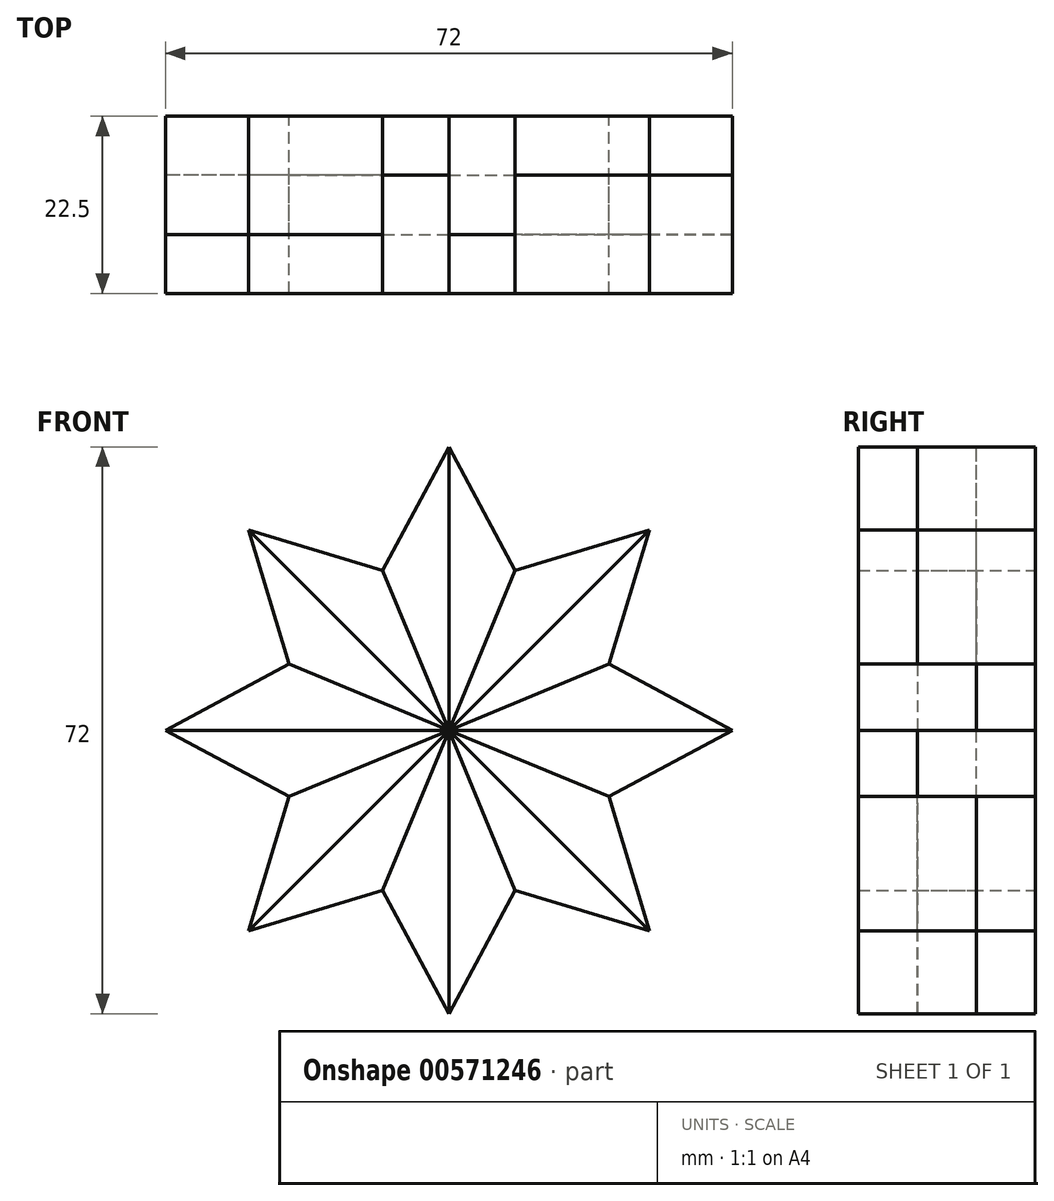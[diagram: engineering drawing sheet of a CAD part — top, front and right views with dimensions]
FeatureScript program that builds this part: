
annotation { "Feature Type Name" : "Feature", "Feature Type Description" : "" }
export const myFeature = defineFeature(function(context is Context, id is Id, definition is map)
    precondition{}
    {
        {
            var Q0;
            Q0=qCreatedBy(makeId("Front.planeOp"),FACE);
            var sketch = newSketch(context, id + "F0", { "sketchPlane" : qUnion([Q0])});
            skLineSegment(sketch, "E0", {"start": v(0, 0) * mm, "end": v(0, 36) * mm});
            skLineSegment(sketch, "E1", {"start": v(0, 0) * mm, "end": v(8.42, 20.33) * mm});
            skLineSegment(sketch, "E2", {"start": v(0, 36) * mm, "end": v(8.42, 20.33) * mm});
            skLineSegment(sketch, "E3", {"start": v(-8.42, 20.33) * mm, "end": v(0, 0) * mm});
            skLineSegment(sketch, "E4", {"start": v(-8.42, 20.33) * mm, "end": v(0, 36) * mm});
            skLineSegment(sketch, "E5", {"start": v(0.76, 1.83) * mm, "end": v(0.76, 34.59) * mm});
            skLineSegment(sketch, "E6.0.1.0", {"start": v(1.95, 4.7) * mm, "end": v(1.95, 32.37) * mm});
            skLineSegment(sketch, "E6.0.2.0", {"start": v(3.14, 7.57) * mm, "end": v(3.14, 30.16) * mm});
            skLineSegment(sketch, "E6.0.3.0", {"start": v(4.33, 10.44) * mm, "end": v(4.33, 27.95) * mm});
            skLineSegment(sketch, "E6.0.4.0", {"start": v(5.51, 13.31) * mm, "end": v(5.51, 25.73) * mm});
            skLineSegment(sketch, "E6.0.5.0", {"start": v(6.7, 16.18) * mm, "end": v(6.7, 23.52) * mm});
            skLineSegment(sketch, "E6.0.6.0", {"start": v(7.9, 19.05) * mm, "end": v(7.9, 21.3) * mm});
            skLineSegment(sketch, "E7.1.0", {"start": v(-5.51, 13.31) * mm, "end": v(-14.3, 22.1) * mm});
            skLineSegment(sketch, "E7.1.1", {"start": v(-6.7, 16.18) * mm, "end": v(-11.9, 21.37) * mm});
            skLineSegment(sketch, "E7.1.2", {"start": v(0, 0) * mm, "end": v(-8.42, 20.33) * mm});
            skLineSegment(sketch, "E7.1.3", {"start": v(-4.33, 10.44) * mm, "end": v(-16.7, 22.82) * mm});
            skLineSegment(sketch, "E7.1.4", {"start": v(-3.14, 7.57) * mm, "end": v(-19.1, 23.54) * mm});
            skLineSegment(sketch, "E7.1.5", {"start": v(-25.46, 25.46) * mm, "end": v(-8.42, 20.33) * mm});
            skLineSegment(sketch, "E7.1.6", {"start": v(-20.33, 8.42) * mm, "end": v(0, 0) * mm});
            skLineSegment(sketch, "E7.1.7", {"start": v(-1.95, 4.7) * mm, "end": v(-21.52, 24.27) * mm});
            skLineSegment(sketch, "E7.1.8", {"start": v(-0.76, 1.83) * mm, "end": v(-23.92, 25) * mm});
            skLineSegment(sketch, "E7.1.9", {"start": v(-20.33, 8.42) * mm, "end": v(-25.46, 25.46) * mm});
            skLineSegment(sketch, "E7.1.10", {"start": v(0, 0) * mm, "end": v(-25.46, 25.46) * mm});
            skLineSegment(sketch, "E7.1.11", {"start": v(-7.9, 19.05) * mm, "end": v(-9.49, 20.65) * mm});
            skLineSegment(sketch, "E7.2.0", {"start": v(-13.31, 5.51) * mm, "end": v(-25.73, 5.51) * mm});
            skLineSegment(sketch, "E7.2.1", {"start": v(-16.18, 6.7) * mm, "end": v(-23.52, 6.7) * mm});
            skLineSegment(sketch, "E7.2.2", {"start": v(0, 0) * mm, "end": v(-20.33, 8.42) * mm});
            skLineSegment(sketch, "E7.2.3", {"start": v(-10.44, 4.33) * mm, "end": v(-27.95, 4.33) * mm});
            skLineSegment(sketch, "E7.2.4", {"start": v(-7.57, 3.14) * mm, "end": v(-30.16, 3.14) * mm});
            skLineSegment(sketch, "E7.2.5", {"start": v(-36, 0) * mm, "end": v(-20.33, 8.42) * mm});
            skLineSegment(sketch, "E7.2.6", {"start": v(-20.33, -8.42) * mm, "end": v(0, 0) * mm});
            skLineSegment(sketch, "E7.2.7", {"start": v(-4.7, 1.95) * mm, "end": v(-32.37, 1.95) * mm});
            skLineSegment(sketch, "E7.2.8", {"start": v(-1.83, 0.76) * mm, "end": v(-34.59, 0.76) * mm});
            skLineSegment(sketch, "E7.2.9", {"start": v(-20.33, -8.42) * mm, "end": v(-36, 0) * mm});
            skLineSegment(sketch, "E7.2.10", {"start": v(0, 0) * mm, "end": v(-36, 0) * mm});
            skLineSegment(sketch, "E7.2.11", {"start": v(-19.05, 7.9) * mm, "end": v(-21.3, 7.9) * mm});
            skLineSegment(sketch, "E7.3.0", {"start": v(-13.31, -5.51) * mm, "end": v(-22.1, -14.3) * mm});
            skLineSegment(sketch, "E7.3.1", {"start": v(-16.18, -6.7) * mm, "end": v(-21.37, -11.9) * mm});
            skLineSegment(sketch, "E7.3.2", {"start": v(0, 0) * mm, "end": v(-20.33, -8.42) * mm});
            skLineSegment(sketch, "E7.3.3", {"start": v(-10.44, -4.33) * mm, "end": v(-22.82, -16.7) * mm});
            skLineSegment(sketch, "E7.3.4", {"start": v(-7.57, -3.14) * mm, "end": v(-23.54, -19.1) * mm});
            skLineSegment(sketch, "E7.3.5", {"start": v(-25.46, -25.46) * mm, "end": v(-20.33, -8.42) * mm});
            skLineSegment(sketch, "E7.3.6", {"start": v(-8.42, -20.33) * mm, "end": v(0, 0) * mm});
            skLineSegment(sketch, "E7.3.7", {"start": v(-4.7, -1.95) * mm, "end": v(-24.27, -21.52) * mm});
            skLineSegment(sketch, "E7.3.8", {"start": v(-1.83, -0.76) * mm, "end": v(-25, -23.92) * mm});
            skLineSegment(sketch, "E7.3.9", {"start": v(-8.42, -20.33) * mm, "end": v(-25.46, -25.46) * mm});
            skLineSegment(sketch, "E7.3.10", {"start": v(0, 0) * mm, "end": v(-25.46, -25.46) * mm});
            skLineSegment(sketch, "E7.3.11", {"start": v(-19.05, -7.9) * mm, "end": v(-20.65, -9.49) * mm});
            skLineSegment(sketch, "E7.4.0", {"start": v(-5.51, -13.31) * mm, "end": v(-5.51, -25.73) * mm});
            skLineSegment(sketch, "E7.4.1", {"start": v(-6.7, -16.18) * mm, "end": v(-6.7, -23.52) * mm});
            skLineSegment(sketch, "E7.4.2", {"start": v(0, 0) * mm, "end": v(-8.42, -20.33) * mm});
            skLineSegment(sketch, "E7.4.3", {"start": v(-4.33, -10.44) * mm, "end": v(-4.33, -27.95) * mm});
            skLineSegment(sketch, "E7.4.4", {"start": v(-3.14, -7.57) * mm, "end": v(-3.14, -30.16) * mm});
            skLineSegment(sketch, "E7.4.5", {"start": v(0, -36) * mm, "end": v(-8.42, -20.33) * mm});
            skLineSegment(sketch, "E7.4.6", {"start": v(8.42, -20.33) * mm, "end": v(0, 0) * mm});
            skLineSegment(sketch, "E7.4.7", {"start": v(-1.95, -4.7) * mm, "end": v(-1.95, -32.37) * mm});
            skLineSegment(sketch, "E7.4.8", {"start": v(-0.76, -1.83) * mm, "end": v(-0.76, -34.59) * mm});
            skLineSegment(sketch, "E7.4.9", {"start": v(8.42, -20.33) * mm, "end": v(0, -36) * mm});
            skLineSegment(sketch, "E7.4.10", {"start": v(0, 0) * mm, "end": v(0, -36) * mm});
            skLineSegment(sketch, "E7.4.11", {"start": v(-7.9, -19.05) * mm, "end": v(-7.9, -21.3) * mm});
            skLineSegment(sketch, "E7.5.0", {"start": v(5.51, -13.31) * mm, "end": v(14.3, -22.1) * mm});
            skLineSegment(sketch, "E7.5.1", {"start": v(6.7, -16.18) * mm, "end": v(11.9, -21.37) * mm});
            skLineSegment(sketch, "E7.5.2", {"start": v(0, 0) * mm, "end": v(8.42, -20.33) * mm});
            skLineSegment(sketch, "E7.5.3", {"start": v(4.33, -10.44) * mm, "end": v(16.7, -22.82) * mm});
            skLineSegment(sketch, "E7.5.4", {"start": v(3.14, -7.57) * mm, "end": v(19.1, -23.54) * mm});
            skLineSegment(sketch, "E7.5.5", {"start": v(25.46, -25.46) * mm, "end": v(8.42, -20.33) * mm});
            skLineSegment(sketch, "E7.5.6", {"start": v(20.33, -8.42) * mm, "end": v(0, 0) * mm});
            skLineSegment(sketch, "E7.5.7", {"start": v(1.95, -4.7) * mm, "end": v(21.52, -24.27) * mm});
            skLineSegment(sketch, "E7.5.8", {"start": v(0.76, -1.83) * mm, "end": v(23.92, -25) * mm});
            skLineSegment(sketch, "E7.5.9", {"start": v(20.33, -8.42) * mm, "end": v(25.46, -25.46) * mm});
            skLineSegment(sketch, "E7.5.10", {"start": v(0, 0) * mm, "end": v(25.46, -25.46) * mm});
            skLineSegment(sketch, "E7.5.11", {"start": v(7.9, -19.05) * mm, "end": v(9.49, -20.65) * mm});
            skLineSegment(sketch, "E7.6.0", {"start": v(13.31, -5.51) * mm, "end": v(25.73, -5.51) * mm});
            skLineSegment(sketch, "E7.6.1", {"start": v(16.18, -6.7) * mm, "end": v(23.52, -6.7) * mm});
            skLineSegment(sketch, "E7.6.2", {"start": v(0, 0) * mm, "end": v(20.33, -8.42) * mm});
            skLineSegment(sketch, "E7.6.3", {"start": v(10.44, -4.33) * mm, "end": v(27.95, -4.33) * mm});
            skLineSegment(sketch, "E7.6.4", {"start": v(7.57, -3.14) * mm, "end": v(30.16, -3.14) * mm});
            skLineSegment(sketch, "E7.6.5", {"start": v(36, 0) * mm, "end": v(20.33, -8.42) * mm});
            skLineSegment(sketch, "E7.6.6", {"start": v(20.33, 8.42) * mm, "end": v(0, 0) * mm});
            skLineSegment(sketch, "E7.6.7", {"start": v(4.7, -1.95) * mm, "end": v(32.37, -1.95) * mm});
            skLineSegment(sketch, "E7.6.8", {"start": v(1.83, -0.76) * mm, "end": v(34.59, -0.76) * mm});
            skLineSegment(sketch, "E7.6.9", {"start": v(20.33, 8.42) * mm, "end": v(36, 0) * mm});
            skLineSegment(sketch, "E7.6.10", {"start": v(0, 0) * mm, "end": v(36, 0) * mm});
            skLineSegment(sketch, "E7.6.11", {"start": v(19.05, -7.9) * mm, "end": v(21.3, -7.9) * mm});
            skLineSegment(sketch, "E7.7.0", {"start": v(13.31, 5.51) * mm, "end": v(22.1, 14.3) * mm});
            skLineSegment(sketch, "E7.7.1", {"start": v(16.18, 6.7) * mm, "end": v(21.37, 11.9) * mm});
            skLineSegment(sketch, "E7.7.2", {"start": v(0, 0) * mm, "end": v(20.33, 8.42) * mm});
            skLineSegment(sketch, "E7.7.3", {"start": v(10.44, 4.33) * mm, "end": v(22.82, 16.7) * mm});
            skLineSegment(sketch, "E7.7.4", {"start": v(7.57, 3.14) * mm, "end": v(23.54, 19.1) * mm});
            skLineSegment(sketch, "E7.7.5", {"start": v(25.46, 25.46) * mm, "end": v(20.33, 8.42) * mm});
            skLineSegment(sketch, "E7.7.6", {"start": v(8.42, 20.33) * mm, "end": v(0, 0) * mm});
            skLineSegment(sketch, "E7.7.7", {"start": v(4.7, 1.95) * mm, "end": v(24.27, 21.52) * mm});
            skLineSegment(sketch, "E7.7.8", {"start": v(1.83, 0.76) * mm, "end": v(25, 23.92) * mm});
            skLineSegment(sketch, "E7.7.9", {"start": v(8.42, 20.33) * mm, "end": v(25.46, 25.46) * mm});
            skLineSegment(sketch, "E7.7.10", {"start": v(0, 0) * mm, "end": v(25.46, 25.46) * mm});
            skLineSegment(sketch, "E7.7.11", {"start": v(19.05, 7.9) * mm, "end": v(20.65, 9.49) * mm});
            skPoint(sketch, "E7.center", {"position": v(0, 0) * mm});
            skSolve(sketch);
        }
        {
            var Q0;
            {var subQ0=sQuery(id+"F0.wireOp",EDGE,"E7.7.7");Q0=makeQuery(id+"F0.imprint","IMPRINT",FACE,{"disambiguationData":[TD([[makeQuery(id+"F0.imprint","IMPRINT",EDGE,{"derivedFrom":subQ0}),1.0]])]});}
            var Q1;
            {var subQ0=sQuery(id+"F0.wireOp",EDGE,"E7.1.7");Q1=makeQuery(id+"F0.imprint","IMPRINT",FACE,{"disambiguationData":[TD([[makeQuery(id+"F0.imprint","IMPRINT",EDGE,{"derivedFrom":subQ0}),1.0]])]});}
            var Q2;
            {var subQ0=sQuery(id+"F0.wireOp",EDGE,"E7.3.7");Q2=makeQuery(id+"F0.imprint","IMPRINT",FACE,{"disambiguationData":[TD([[makeQuery(id+"F0.imprint","IMPRINT",EDGE,{"derivedFrom":subQ0}),1.0]])]});}
            var Q3;
            {var subQ0=sQuery(id+"F0.wireOp",EDGE,"E7.1.0");Q3=makeQuery(id+"F0.imprint","IMPRINT",FACE,{"disambiguationData":[TD([[makeQuery(id+"F0.imprint","IMPRINT",EDGE,{"derivedFrom":subQ0}),-1.0]])]});}
            var Q4;
            {var subQ0=sQuery(id+"F0.wireOp",EDGE,"E7.6.0");Q4=makeQuery(id+"F0.imprint","IMPRINT",FACE,{"disambiguationData":[TD([[makeQuery(id+"F0.imprint","IMPRINT",EDGE,{"derivedFrom":subQ0}),-1.0]])]});}
            var Q5;
            {var subQ0=sQuery(id+"F0.wireOp",EDGE,"E7.2.4");Q5=makeQuery(id+"F0.imprint","IMPRINT",FACE,{"disambiguationData":[TD([[makeQuery(id+"F0.imprint","IMPRINT",EDGE,{"derivedFrom":subQ0}),1.0]])]});}
            var Q6;
            {var subQ0=sQuery(id+"F0.wireOp",EDGE,"E7.5.0");Q6=makeQuery(id+"F0.imprint","IMPRINT",FACE,{"disambiguationData":[TD([[makeQuery(id+"F0.imprint","IMPRINT",EDGE,{"derivedFrom":subQ0}),-1.0]])]});}
            var Q7;
            {var subQ0=sQuery(id+"F0.wireOp",EDGE,"E7.5.1");Q7=makeQuery(id+"F0.imprint","IMPRINT",FACE,{"disambiguationData":[TD([[makeQuery(id+"F0.imprint","IMPRINT",EDGE,{"derivedFrom":subQ0}),-1.0]])]});}
            var Q8;
            {var subQ0=sQuery(id+"F0.wireOp",EDGE,"E7.2.3");Q8=makeQuery(id+"F0.imprint","IMPRINT",FACE,{"disambiguationData":[TD([[makeQuery(id+"F0.imprint","IMPRINT",EDGE,{"derivedFrom":subQ0}),1.0]])]});}
            var Q9;
            {var subQ2=sQuery(id+"F0.wireOp",EDGE,"E7.6.8");Q9=makeQuery(id+"F0.imprint","IMPRINT",FACE,{"disambiguationData":[TD([[makeQuery(id+"F0.imprint","IMPRINT",EDGE,{"derivedFrom":subQ2}),1.0]])]});}
            var Q10;
            {var subQ0=sQuery(id+"F0.wireOp",EDGE,"E7.4.0");Q10=makeQuery(id+"F0.imprint","IMPRINT",FACE,{"disambiguationData":[TD([[makeQuery(id+"F0.imprint","IMPRINT",EDGE,{"derivedFrom":subQ0}),1.0]])]});}
            var Q11;
            {var subQ0=sQuery(id+"F0.wireOp",EDGE,"E7.4.4");Q11=makeQuery(id+"F0.imprint","IMPRINT",FACE,{"disambiguationData":[TD([[makeQuery(id+"F0.imprint","IMPRINT",EDGE,{"derivedFrom":subQ0}),1.0]])]});}
            var Q12;
            {var subQ0=sQuery(id+"F0.wireOp",EDGE,"E7.2.0");Q12=makeQuery(id+"F0.imprint","IMPRINT",FACE,{"disambiguationData":[TD([[makeQuery(id+"F0.imprint","IMPRINT",EDGE,{"derivedFrom":subQ0}),-1.0]])]});}
            var Q13;
            {var subQ0=sQuery(id+"F0.wireOp",EDGE,"E7.1.1");Q13=makeQuery(id+"F0.imprint","IMPRINT",FACE,{"disambiguationData":[TD([[makeQuery(id+"F0.imprint","IMPRINT",EDGE,{"derivedFrom":subQ0}),-1.0]])]});}
            var Q14;
            {var subQ0=sQuery(id+"F0.wireOp",EDGE,"E7.6.4");Q14=makeQuery(id+"F0.imprint","IMPRINT",FACE,{"disambiguationData":[TD([[makeQuery(id+"F0.imprint","IMPRINT",EDGE,{"derivedFrom":subQ0}),1.0]])]});}
            var Q15;
            {var subQ2=sQuery(id+"F0.wireOp",EDGE,"E7.1.8");Q15=makeQuery(id+"F0.imprint","IMPRINT",FACE,{"disambiguationData":[TD([[makeQuery(id+"F0.imprint","IMPRINT",EDGE,{"derivedFrom":subQ2}),1.0]])]});}
            var Q16;
            {var subQ0=sQuery(id+"F0.wireOp",EDGE,"E7.2.0");Q16=makeQuery(id+"F0.imprint","IMPRINT",FACE,{"disambiguationData":[TD([[makeQuery(id+"F0.imprint","IMPRINT",EDGE,{"derivedFrom":subQ0}),1.0]])]});}
            var Q17;
            {var subQ2=sQuery(id+"F0.wireOp",EDGE,"E7.4.8");Q17=makeQuery(id+"F0.imprint","IMPRINT",FACE,{"disambiguationData":[TD([[makeQuery(id+"F0.imprint","IMPRINT",EDGE,{"derivedFrom":subQ2}),1.0]])]});}
            var Q18;
            {var subQ0=sQuery(id+"F0.wireOp",EDGE,"E7.4.1");Q18=makeQuery(id+"F0.imprint","IMPRINT",FACE,{"disambiguationData":[TD([[makeQuery(id+"F0.imprint","IMPRINT",EDGE,{"derivedFrom":subQ0}),-1.0]])]});}
            var Q19;
            {var subQ0=sQuery(id+"F0.wireOp",EDGE,"E7.6.7");Q19=makeQuery(id+"F0.imprint","IMPRINT",FACE,{"disambiguationData":[TD([[makeQuery(id+"F0.imprint","IMPRINT",EDGE,{"derivedFrom":subQ0}),1.0]])]});}
            var Q20;
            {var subQ0=sQuery(id+"F0.wireOp",EDGE,"E7.5.0");Q20=makeQuery(id+"F0.imprint","IMPRINT",FACE,{"disambiguationData":[TD([[makeQuery(id+"F0.imprint","IMPRINT",EDGE,{"derivedFrom":subQ0}),1.0]])]});}
            var Q21;
            {var subQ2=sQuery(id+"F0.wireOp",EDGE,"E7.7.8");Q21=makeQuery(id+"F0.imprint","IMPRINT",FACE,{"disambiguationData":[TD([[makeQuery(id+"F0.imprint","IMPRINT",EDGE,{"derivedFrom":subQ2}),1.0]])]});}
            var Q22;
            {var subQ0=sQuery(id+"F0.wireOp",EDGE,"E7.3.0");Q22=makeQuery(id+"F0.imprint","IMPRINT",FACE,{"disambiguationData":[TD([[makeQuery(id+"F0.imprint","IMPRINT",EDGE,{"derivedFrom":subQ0}),1.0]])]});}
            var Q23;
            {var subQ2=sQuery(id+"F0.wireOp",EDGE,"E7.5.8");Q23=makeQuery(id+"F0.imprint","IMPRINT",FACE,{"disambiguationData":[TD([[makeQuery(id+"F0.imprint","IMPRINT",EDGE,{"derivedFrom":subQ2}),1.0]])]});}
            var Q24;
            {var subQ0=sQuery(id+"F0.wireOp",EDGE,"E7.7.4");Q24=makeQuery(id+"F0.imprint","IMPRINT",FACE,{"disambiguationData":[TD([[makeQuery(id+"F0.imprint","IMPRINT",EDGE,{"derivedFrom":subQ0}),1.0]])]});}
            var Q25;
            {var subQ0=sQuery(id+"F0.wireOp",EDGE,"E7.1.3");Q25=makeQuery(id+"F0.imprint","IMPRINT",FACE,{"disambiguationData":[TD([[makeQuery(id+"F0.imprint","IMPRINT",EDGE,{"derivedFrom":subQ0}),1.0]])]});}
            var Q26;
            {var subQ0=sQuery(id+"F0.wireOp",EDGE,"E7.7.1");Q26=makeQuery(id+"F0.imprint","IMPRINT",FACE,{"disambiguationData":[TD([[makeQuery(id+"F0.imprint","IMPRINT",EDGE,{"derivedFrom":subQ0}),-1.0]])]});}
            var Q27;
            {var subQ0=sQuery(id+"F0.wireOp",EDGE,"E7.6.0");Q27=makeQuery(id+"F0.imprint","IMPRINT",FACE,{"disambiguationData":[TD([[makeQuery(id+"F0.imprint","IMPRINT",EDGE,{"derivedFrom":subQ0}),1.0]])]});}
            var Q28;
            {var subQ0=sQuery(id+"F0.wireOp",EDGE,"E7.3.0");Q28=makeQuery(id+"F0.imprint","IMPRINT",FACE,{"disambiguationData":[TD([[makeQuery(id+"F0.imprint","IMPRINT",EDGE,{"derivedFrom":subQ0}),-1.0]])]});}
            var Q29;
            {var subQ0=sQuery(id+"F0.wireOp",EDGE,"E7.1.4");Q29=makeQuery(id+"F0.imprint","IMPRINT",FACE,{"disambiguationData":[TD([[makeQuery(id+"F0.imprint","IMPRINT",EDGE,{"derivedFrom":subQ0}),1.0]])]});}
            var Q30;
            {var subQ0=sQuery(id+"F0.wireOp",EDGE,"E7.4.0");Q30=makeQuery(id+"F0.imprint","IMPRINT",FACE,{"disambiguationData":[TD([[makeQuery(id+"F0.imprint","IMPRINT",EDGE,{"derivedFrom":subQ0}),-1.0]])]});}
            var Q31;
            {var subQ0=sQuery(id+"F0.wireOp",EDGE,"E7.2.7");Q31=makeQuery(id+"F0.imprint","IMPRINT",FACE,{"disambiguationData":[TD([[makeQuery(id+"F0.imprint","IMPRINT",EDGE,{"derivedFrom":subQ0}),1.0]])]});}
            var Q32;
            {var subQ0=sQuery(id+"F0.wireOp",EDGE,"E7.6.1");Q32=makeQuery(id+"F0.imprint","IMPRINT",FACE,{"disambiguationData":[TD([[makeQuery(id+"F0.imprint","IMPRINT",EDGE,{"derivedFrom":subQ0}),-1.0]])]});}
            var Q33;
            {var subQ0=sQuery(id+"F0.wireOp",EDGE,"E7.7.0");Q33=makeQuery(id+"F0.imprint","IMPRINT",FACE,{"disambiguationData":[TD([[makeQuery(id+"F0.imprint","IMPRINT",EDGE,{"derivedFrom":subQ0}),1.0]])]});}
            var Q34;
            {var subQ0=sQuery(id+"F0.wireOp",EDGE,"E7.4.3");Q34=makeQuery(id+"F0.imprint","IMPRINT",FACE,{"disambiguationData":[TD([[makeQuery(id+"F0.imprint","IMPRINT",EDGE,{"derivedFrom":subQ0}),1.0]])]});}
            var Q35;
            {var subQ0=sQuery(id+"F0.wireOp",EDGE,"E7.3.3");Q35=makeQuery(id+"F0.imprint","IMPRINT",FACE,{"disambiguationData":[TD([[makeQuery(id+"F0.imprint","IMPRINT",EDGE,{"derivedFrom":subQ0}),1.0]])]});}
            var Q36;
            {var subQ0=sQuery(id+"F0.wireOp",EDGE,"E6.0.5.0");Q36=makeQuery(id+"F0.imprint","IMPRINT",FACE,{"disambiguationData":[TD([[makeQuery(id+"F0.imprint","IMPRINT",EDGE,{"derivedFrom":subQ0}),-1.0]])]});}
            var Q37;
            {var subQ0=sQuery(id+"F0.wireOp",EDGE,"E7.5.3");Q37=makeQuery(id+"F0.imprint","IMPRINT",FACE,{"disambiguationData":[TD([[makeQuery(id+"F0.imprint","IMPRINT",EDGE,{"derivedFrom":subQ0}),1.0]])]});}
            var Q38;
            {var subQ0=sQuery(id+"F0.wireOp",EDGE,"E7.7.3");Q38=makeQuery(id+"F0.imprint","IMPRINT",FACE,{"disambiguationData":[TD([[makeQuery(id+"F0.imprint","IMPRINT",EDGE,{"derivedFrom":subQ0}),1.0]])]});}
            var Q39;
            {var subQ0=sQuery(id+"F0.wireOp",EDGE,"E7.2.1");Q39=makeQuery(id+"F0.imprint","IMPRINT",FACE,{"disambiguationData":[TD([[makeQuery(id+"F0.imprint","IMPRINT",EDGE,{"derivedFrom":subQ0}),-1.0]])]});}
            var Q40;
            {var subQ0=sQuery(id+"F0.wireOp",EDGE,"E6.0.3.0");Q40=makeQuery(id+"F0.imprint","IMPRINT",FACE,{"disambiguationData":[TD([[makeQuery(id+"F0.imprint","IMPRINT",EDGE,{"derivedFrom":subQ0}),-1.0]])]});}
            var Q41;
            {var subQ0=sQuery(id+"F0.wireOp",EDGE,"E6.0.4.0");Q41=makeQuery(id+"F0.imprint","IMPRINT",FACE,{"disambiguationData":[TD([[makeQuery(id+"F0.imprint","IMPRINT",EDGE,{"derivedFrom":subQ0}),-1.0]])]});}
            var Q42;
            {var subQ0=sQuery(id+"F0.wireOp",EDGE,"E7.3.4");Q42=makeQuery(id+"F0.imprint","IMPRINT",FACE,{"disambiguationData":[TD([[makeQuery(id+"F0.imprint","IMPRINT",EDGE,{"derivedFrom":subQ0}),1.0]])]});}
            var Q43;
            {var subQ0=sQuery(id+"F0.wireOp",EDGE,"E5");Q43=makeQuery(id+"F0.imprint","IMPRINT",FACE,{"disambiguationData":[TD([[makeQuery(id+"F0.imprint","IMPRINT",EDGE,{"derivedFrom":subQ0}),-1.0]])]});}
            var Q44;
            {var subQ0=sQuery(id+"F0.wireOp",EDGE,"E6.0.1.0");Q44=makeQuery(id+"F0.imprint","IMPRINT",FACE,{"disambiguationData":[TD([[makeQuery(id+"F0.imprint","IMPRINT",EDGE,{"derivedFrom":subQ0}),-1.0]])]});}
            var Q45;
            {var subQ0=sQuery(id+"F0.wireOp",EDGE,"E7.5.7");Q45=makeQuery(id+"F0.imprint","IMPRINT",FACE,{"disambiguationData":[TD([[makeQuery(id+"F0.imprint","IMPRINT",EDGE,{"derivedFrom":subQ0}),1.0]])]});}
            var Q46;
            {var subQ0=sQuery(id+"F0.wireOp",EDGE,"E7.6.3");Q46=makeQuery(id+"F0.imprint","IMPRINT",FACE,{"disambiguationData":[TD([[makeQuery(id+"F0.imprint","IMPRINT",EDGE,{"derivedFrom":subQ0}),1.0]])]});}
            var Q47;
            {var subQ0=sQuery(id+"F0.wireOp",EDGE,"E7.3.1");Q47=makeQuery(id+"F0.imprint","IMPRINT",FACE,{"disambiguationData":[TD([[makeQuery(id+"F0.imprint","IMPRINT",EDGE,{"derivedFrom":subQ0}),-1.0]])]});}
            var Q48;
            {var subQ0=sQuery(id+"F0.wireOp",EDGE,"E6.0.2.0");Q48=makeQuery(id+"F0.imprint","IMPRINT",FACE,{"disambiguationData":[TD([[makeQuery(id+"F0.imprint","IMPRINT",EDGE,{"derivedFrom":subQ0}),-1.0]])]});}
            var Q49;
            {var subQ0=sQuery(id+"F0.wireOp",EDGE,"E7.5.4");Q49=makeQuery(id+"F0.imprint","IMPRINT",FACE,{"disambiguationData":[TD([[makeQuery(id+"F0.imprint","IMPRINT",EDGE,{"derivedFrom":subQ0}),1.0]])]});}
            var Q50;
            {var subQ2=sQuery(id+"F0.wireOp",EDGE,"E7.3.8");Q50=makeQuery(id+"F0.imprint","IMPRINT",FACE,{"disambiguationData":[TD([[makeQuery(id+"F0.imprint","IMPRINT",EDGE,{"derivedFrom":subQ2}),1.0]])]});}
            var Q51;
            {var subQ2=sQuery(id+"F0.wireOp",EDGE,"E7.2.8");Q51=makeQuery(id+"F0.imprint","IMPRINT",FACE,{"disambiguationData":[TD([[makeQuery(id+"F0.imprint","IMPRINT",EDGE,{"derivedFrom":subQ2}),1.0]])]});}
            var Q52;
            {var subQ0=sQuery(id+"F0.wireOp",EDGE,"E7.1.0");Q52=makeQuery(id+"F0.imprint","IMPRINT",FACE,{"disambiguationData":[TD([[makeQuery(id+"F0.imprint","IMPRINT",EDGE,{"derivedFrom":subQ0}),1.0]])]});}
            var Q53;
            {var subQ0=sQuery(id+"F0.wireOp",EDGE,"E0");Q53=makeQuery(id+"F0.imprint","IMPRINT",FACE,{"disambiguationData":[TD([[makeQuery(id+"F0.imprint","IMPRINT",EDGE,{"derivedFrom":subQ0}),-1.0]])]});}
            var Q54;
            {var subQ0=sQuery(id+"F0.wireOp",EDGE,"E7.7.0");Q54=makeQuery(id+"F0.imprint","IMPRINT",FACE,{"disambiguationData":[TD([[makeQuery(id+"F0.imprint","IMPRINT",EDGE,{"derivedFrom":subQ0}),-1.0]])]});}
            var Q55;
            {var subQ0=sQuery(id+"F0.wireOp",EDGE,"E7.4.7");Q55=makeQuery(id+"F0.imprint","IMPRINT",FACE,{"disambiguationData":[TD([[makeQuery(id+"F0.imprint","IMPRINT",EDGE,{"derivedFrom":subQ0}),1.0]])]});}
            var Q56;
            {var subQ3=sQuery(id+"F0.wireOp",EDGE,"E7.6.11");Q56=makeQuery(id+"F0.imprint","IMPRINT",FACE,{"disambiguationData":[TD([[makeQuery(id+"F0.imprint","IMPRINT",EDGE,{"derivedFrom":subQ3}),-1.0]])]});}
            var Q57;
            {var subQ3=sQuery(id+"F0.wireOp",EDGE,"E7.4.11");Q57=makeQuery(id+"F0.imprint","IMPRINT",FACE,{"disambiguationData":[TD([[makeQuery(id+"F0.imprint","IMPRINT",EDGE,{"derivedFrom":subQ3}),-1.0]])]});}
            var Q58;
            {var subQ3=sQuery(id+"F0.wireOp",EDGE,"E7.2.11");Q58=makeQuery(id+"F0.imprint","IMPRINT",FACE,{"disambiguationData":[TD([[makeQuery(id+"F0.imprint","IMPRINT",EDGE,{"derivedFrom":subQ3}),-1.0]])]});}
            var Q59;
            {var subQ3=sQuery(id+"F0.wireOp",EDGE,"E7.1.11");Q59=makeQuery(id+"F0.imprint","IMPRINT",FACE,{"disambiguationData":[TD([[makeQuery(id+"F0.imprint","IMPRINT",EDGE,{"derivedFrom":subQ3}),-1.0]])]});}
            var Q60;
            {var subQ3=sQuery(id+"F0.wireOp",EDGE,"E7.3.11");Q60=makeQuery(id+"F0.imprint","IMPRINT",FACE,{"disambiguationData":[TD([[makeQuery(id+"F0.imprint","IMPRINT",EDGE,{"derivedFrom":subQ3}),-1.0]])]});}
            var Q61;
            {var subQ3=sQuery(id+"F0.wireOp",EDGE,"E7.7.11");Q61=makeQuery(id+"F0.imprint","IMPRINT",FACE,{"disambiguationData":[TD([[makeQuery(id+"F0.imprint","IMPRINT",EDGE,{"derivedFrom":subQ3}),-1.0]])]});}
            var Q62;
            {var subQ3=sQuery(id+"F0.wireOp",EDGE,"E6.0.6.0");Q62=makeQuery(id+"F0.imprint","IMPRINT",FACE,{"disambiguationData":[TD([[makeQuery(id+"F0.imprint","IMPRINT",EDGE,{"derivedFrom":subQ3}),-1.0]])]});}
            var Q63;
            {var subQ3=sQuery(id+"F0.wireOp",EDGE,"E7.5.11");Q63=makeQuery(id+"F0.imprint","IMPRINT",FACE,{"disambiguationData":[TD([[makeQuery(id+"F0.imprint","IMPRINT",EDGE,{"derivedFrom":subQ3}),-1.0]])]});}
            extrude(context, id + "F1", {"entities" : qUnion([Q0, Q1, Q2, Q3, Q4, Q5, Q6, Q7, Q8, Q9, Q10, Q11, Q12, Q13, Q14, Q15, Q16, Q17, Q18, Q19, Q20, Q21, Q22, Q23, Q24, Q25, Q26, Q27, Q28, Q29, Q30, Q31, Q32, Q33, Q34, Q35, Q36, Q37, Q38, Q39, Q40, Q41, Q42, Q43, Q44, Q45, Q46, Q47, Q48, Q49, Q50, Q51, Q52, Q53, Q54, Q55, Q56, Q57, Q58, Q59, Q60, Q61, Q62, Q63]), "endBound" : BoundingType.SYMMETRIC, "depth" : 15 * mm, "offsetDistance" : 25 * mm});
        }
        {
            var Q0;
            {var subQ5=sQuery(id+"F0.wireOp",EDGE,"E7.7.9");Q0=makeQuery(id+"F0.imprint","IMPRINT",FACE,{"disambiguationData":[TD([[makeQuery(id+"F0.imprint","IMPRINT",EDGE,{"derivedFrom":subQ5}),-1.0]])]});}
            var Q1;
            {var subQ1=sQuery(id+"F0.wireOp",EDGE,"E0");Q1=makeQuery(id+"F0.imprint","IMPRINT",FACE,{"disambiguationData":[TD([[makeQuery(id+"F0.imprint","IMPRINT",EDGE,{"derivedFrom":subQ1}),1.0]])]});}
            var Q2;
            {var subQ4=sQuery(id+"F0.wireOp",EDGE,"E7.1.9");Q2=makeQuery(id+"F0.imprint","IMPRINT",FACE,{"disambiguationData":[TD([[makeQuery(id+"F0.imprint","IMPRINT",EDGE,{"derivedFrom":subQ4}),-1.0]])]});}
            var Q3;
            {var subQ4=sQuery(id+"F0.wireOp",EDGE,"E7.2.9");Q3=makeQuery(id+"F0.imprint","IMPRINT",FACE,{"disambiguationData":[TD([[makeQuery(id+"F0.imprint","IMPRINT",EDGE,{"derivedFrom":subQ4}),-1.0]])]});}
            var Q4;
            {var subQ4=sQuery(id+"F0.wireOp",EDGE,"E7.3.9");Q4=makeQuery(id+"F0.imprint","IMPRINT",FACE,{"disambiguationData":[TD([[makeQuery(id+"F0.imprint","IMPRINT",EDGE,{"derivedFrom":subQ4}),-1.0]])]});}
            var Q5;
            {var subQ4=sQuery(id+"F0.wireOp",EDGE,"E7.5.9");Q5=makeQuery(id+"F0.imprint","IMPRINT",FACE,{"disambiguationData":[TD([[makeQuery(id+"F0.imprint","IMPRINT",EDGE,{"derivedFrom":subQ4}),-1.0]])]});}
            var Q6;
            {var subQ4=sQuery(id+"F0.wireOp",EDGE,"E7.6.9");Q6=makeQuery(id+"F0.imprint","IMPRINT",FACE,{"disambiguationData":[TD([[makeQuery(id+"F0.imprint","IMPRINT",EDGE,{"derivedFrom":subQ4}),-1.0]])]});}
            var Q7;
            {var subQ4=sQuery(id+"F0.wireOp",EDGE,"E7.4.9");Q7=makeQuery(id+"F0.imprint","IMPRINT",FACE,{"disambiguationData":[TD([[makeQuery(id+"F0.imprint","IMPRINT",EDGE,{"derivedFrom":subQ4}),-1.0]])]});}
            extrude(context, id + "F2", {"entities" : qUnion([Q0, Q1, Q2, Q3, Q4, Q5, Q6, Q7]), "depth" : 15 * mm, "offsetDistance" : 25 * mm});
        }
    });
